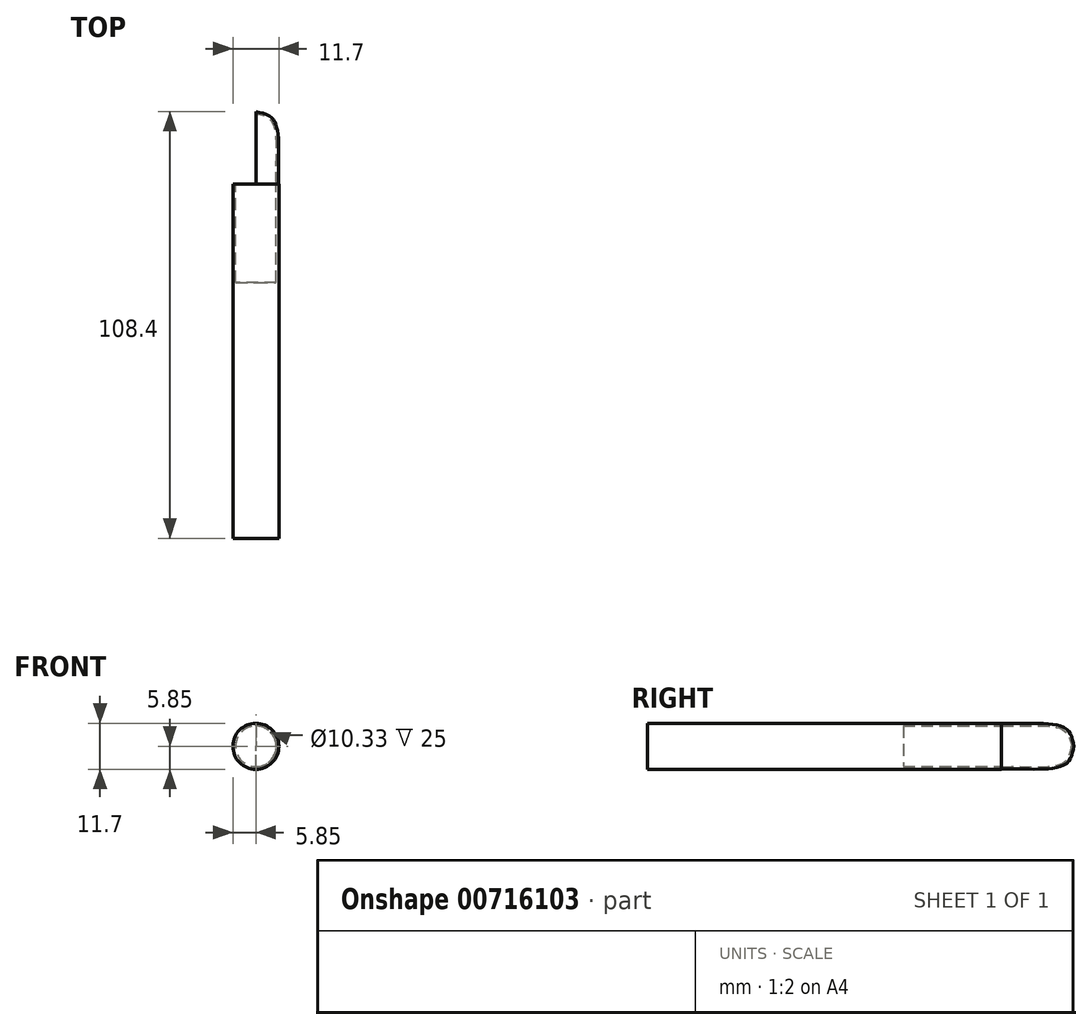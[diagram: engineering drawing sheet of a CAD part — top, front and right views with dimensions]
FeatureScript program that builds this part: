
annotation { "Feature Type Name" : "Feature", "Feature Type Description" : "" }
export const myFeature = defineFeature(function(context is Context, id is Id, definition is map)
    precondition{}
    {
        {
            var Q0;
            Q0=qCreatedBy(makeId("Front.planeOp"),FACE);
            var sketch = newSketch(context, id + "F0", { "sketchPlane" : qUnion([Q0])});
            skCircle(sketch, "E0", {"center": v(0, 0) * mm, "radius": 5.85 * mm});
            skSolve(sketch);
        }
        {
            var Q0;
            Q0 = qSketchRegion(id + "F0", true);
            extrude(context, id + "F1", {"entities" : qUnion([Q0]), "depth" : 90 * mm, "offsetDistance" : 25 * mm});
        }
        {
            var Q0;
            Q0=qCreatedBy(makeId("Top.planeOp"),FACE);
            var sketch = newSketch(context, id + "F2", { "sketchPlane" : qUnion([Q0])});
            skLineSegment(sketch, "E1", {"start": v(0, 0) * mm, "end": v(0, 18.4) * mm});
            skLineSegment(sketch, "E2", {"start": v(0, 0) * mm, "end": v(5.79, 0) * mm});
            skFitSpline(sketch, "E3", {"points": [v(5.79, 0) * mm, v(5.79, 6.42) * mm, v(4.56, 16.18) * mm, v(0, 18.4) * mm], "startDerivative": vector(-0.16, 17.76) * mm, "endDerivative": vector(-18.79, 3.68) * mm});
            skLineSegment(sketch, "E4.0", {"start": v(0.6, 0) * mm, "end": v(0.6, 17.67) * mm});
            skFitSpline(sketch, "E4.1", {"points": [v(5.19, 0) * mm, v(5.18, 0.73) * mm, v(5.17, 1.85) * mm, v(5.16, 3.46) * mm, v(5.17, 4.77) * mm, v(5.18, 6.22) * mm, v(5.2, 7.83) * mm, v(5.21, 9.52) * mm, v(5.16, 11.23) * mm, v(5.01, 12.85) * mm, v(4.74, 14.3) * mm, v(4.39, 15.3) * mm, v(4.04, 15.9) * mm, v(3.63, 16.4) * mm, v(3.02, 16.89) * mm, v(2.1, 17.3) * mm, v(1.05, 17.58) * mm, v(0.28, 17.74) * mm, v(-0.12, 17.81) * mm]});
            skLineSegment(sketch, "E5", {"start": v(0.6, 17.67) * mm, "end": v(0, 17.67) * mm});
            skSolve(sketch);
        }
        {
            var Q0;
            {var subQ4=sQuery(id+"F2.wireOp",EDGE,"E3");Q0=makeQuery(id+"F2.imprint","IMPRINT",FACE,{"disambiguationData":[TD([[makeQuery(id+"F2.imprint","IMPRINT",EDGE,{"derivedFrom":subQ4}),1.0]])]});}
            var Q1;
            Q1=sQuery(id+"F2.wireOp",EDGE,"E1");
            revolve(context, id + "F3", {"operationType" : NewBodyOperationType.ADD, "surfaceOperationType" : NewSurfaceOperationType.NEW, "entities" : qUnion([Q0]), "axis" : qUnion([Q1]), "revolveType" : RevolveType.TWO_DIRECTIONS, "angle" : 90 * degree, "angleBack" : 270 * degree});
        }
        {
            var Q0;
            Q0=makeQuery(id+"F1.opExtrude","CAP_FACE",FACE,{"disambiguationData":[OSD([sQuery(id+"F0.wireOp",EDGE,"E0")])],"isStart":true});
            var sketch = newSketch(context, id + "F4", { "sketchPlane" : qUnion([Q0])});
            skCircle(sketch, "E6", {"center": v(0, 0) * mm, "radius": 5.16 * mm});
            skSolve(sketch);
        }
        {
            var Q0;
            Q0 = qSketchRegion(id + "F4", true);
            extrude(context, id + "F5", {"entities" : qUnion([Q0]), "operationType" : NewBodyOperationType.REMOVE, "oppositeDirection" : true, "depth" : 25 * mm, "offsetDistance" : 25 * mm});
        }
    });
